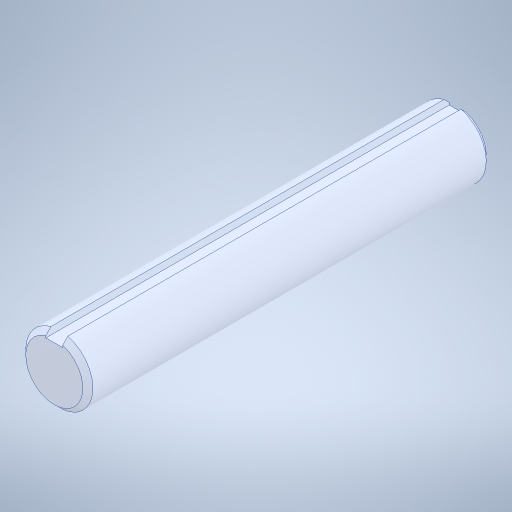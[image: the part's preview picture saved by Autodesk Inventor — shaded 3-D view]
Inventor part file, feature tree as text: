
AUTODESK INVENTOR PART (.ipt)
format: ipt  version: 2023.2 (Build 272271000, 271)  size: 249,344 bytes
history: mixed  units: in
note: dims shown in document units (in); Inventor stores cm internally (conversion verified against a paired STEP export)
features: extrude x1, imported_body x1
ambient origin geometry x8: Origin, YZ Plane, XZ Plane, XY Plane, X Axis, Y Axis, Z Axis, Center Point
bodies: Solid1 (imported_parasolid)
feature tree (2):
  extrude  "Extrude2"  [1 undecoded]
  imported_body  NMx_Import_Brep_tag  [imported B-rep: ~7 faces, bbox_mm=[2.38125, 1.039396, 56.435625]]
note: 1 required parameter value undecoded (feature->parameter linkage not recoverable at this tier; creation-order binding heuristic only, values carry confidence <= 0.55)
